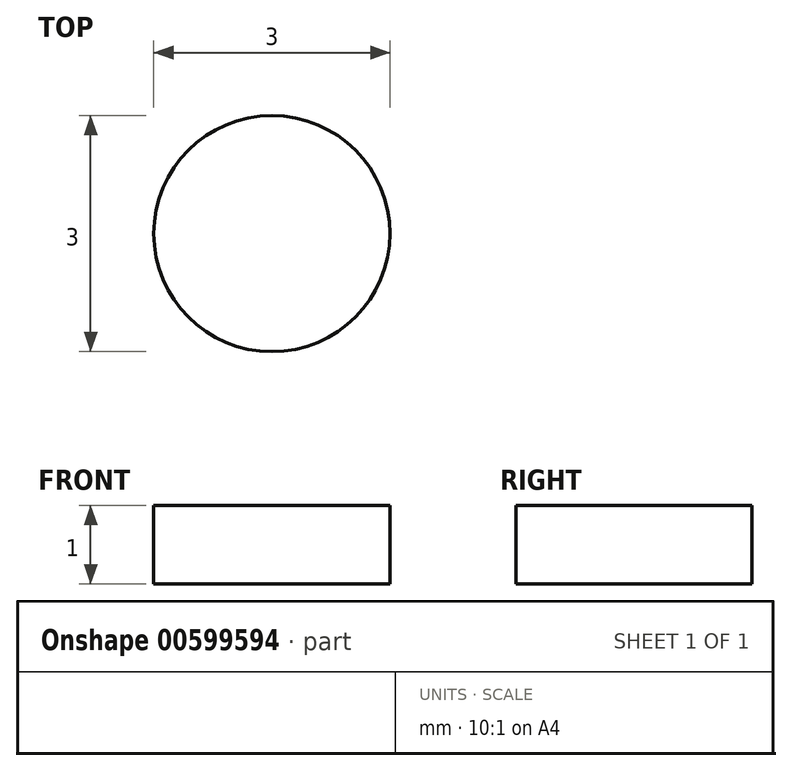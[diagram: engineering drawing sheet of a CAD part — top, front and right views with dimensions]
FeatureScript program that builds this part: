
annotation { "Feature Type Name" : "Feature", "Feature Type Description" : "" }
export const myFeature = defineFeature(function(context is Context, id is Id, definition is map)
    precondition{}
    {
        {
            var Q0;
            Q0=qCreatedBy(makeId("Top.planeOp"),FACE);
            var sketch = newSketch(context, id + "F0", { "sketchPlane" : qUnion([Q0])});
            skLineSegment(sketch, "E0.bottom", {"start": v(13.65, -7.45) * mm, "end": v(-13.65, -7.45) * mm});
            skLineSegment(sketch, "E0.top", {"start": v(13.65, 7.45) * mm, "end": v(-13.65, 7.45) * mm});
            skLineSegment(sketch, "E0.left", {"start": v(16.65, -4.45) * mm, "end": v(16.65, 4.45) * mm});
            skLineSegment(sketch, "E0.right", {"start": v(-16.65, -4.45) * mm, "end": v(-16.65, 4.45) * mm});
            skPoint(sketch, "E0.middle", {"position": v(0, 0) * mm});
            skPoint(sketch, "E1.visualSharp", {"position": v(16.65, 7.45) * mm});
            skArc(sketch, "E1.filletArc", {"start": v(16.65, 4.45) * mm, "mid": v(15.77, 6.57) * mm, "end": v(13.65, 7.45) * mm});
            skPoint(sketch, "E2.visualSharp", {"position": v(16.65, -7.45) * mm});
            skArc(sketch, "E2.filletArc", {"start": v(13.65, -7.45) * mm, "mid": v(15.77, -6.57) * mm, "end": v(16.65, -4.45) * mm});
            skPoint(sketch, "E3.visualSharp", {"position": v(-16.65, -7.45) * mm});
            skArc(sketch, "E3.filletArc", {"start": v(-16.65, -4.45) * mm, "mid": v(-15.77, -6.57) * mm, "end": v(-13.65, -7.45) * mm});
            skPoint(sketch, "E4.visualSharp", {"position": v(-16.65, 7.45) * mm});
            skArc(sketch, "E4.filletArc", {"start": v(-13.65, 7.45) * mm, "mid": v(-15.77, 6.57) * mm, "end": v(-16.65, 4.45) * mm});
            skSolve(sketch);
        }
        {
            var Q0;
            Q0=makeQuery(id+"F0.imprint","IMPRINT",FACE,{"disambiguationData":[TD([[makeQuery(id+"F0.imprint","IMPRINT",EDGE,{"derivedFrom":sQuery(id+"F0.wireOp",EDGE,"E0.bottom")}),-1.0]])]});
            extrude(context, id + "F1", {"entities" : qUnion([Q0]), "depth" : 8 * mm, "offsetDistance" : 25 * mm});
        }
        {
            var Q0;
            Q0=makeQuery(id+"F1.opExtrude","CAP_FACE",FACE,{"disambiguationData":[OSD([sQuery(id+"F0.wireOp",EDGE,"E0.bottom"),sQuery(id+"F0.wireOp",EDGE,"E0.top"),sQuery(id+"F0.wireOp",EDGE,"E0.left"),sQuery(id+"F0.wireOp",EDGE,"E0.right"),sQuery(id+"F0.wireOp",EDGE,"E1.filletArc"),sQuery(id+"F0.wireOp",EDGE,"E2.filletArc"),sQuery(id+"F0.wireOp",EDGE,"E3.filletArc"),sQuery(id+"F0.wireOp",EDGE,"E4.filletArc")])],"isStart":false});
            shell(context, id + "F2", {"entities" : qUnion([Q0]), "thickness" : 1 * mm});
        }
        {
            var Q0;
            Q0=makeQuery(id+"F1.opExtrude","CAP_FACE",FACE,{"disambiguationData":[OSD([sQuery(id+"F0.wireOp",EDGE,"E0.bottom"),sQuery(id+"F0.wireOp",EDGE,"E0.top"),sQuery(id+"F0.wireOp",EDGE,"E0.left"),sQuery(id+"F0.wireOp",EDGE,"E0.right"),sQuery(id+"F0.wireOp",EDGE,"E1.filletArc"),sQuery(id+"F0.wireOp",EDGE,"E2.filletArc"),sQuery(id+"F0.wireOp",EDGE,"E3.filletArc"),sQuery(id+"F0.wireOp",EDGE,"E4.filletArc")])],"isStart":true});
            var sketch = newSketch(context, id + "F3", { "sketchPlane" : qUnion([Q0])});
            skLineSegment(sketch, "E5.bottom", {"start": v(14.5, -8.25) * mm, "end": v(-14.5, -8.25) * mm});
            skLineSegment(sketch, "E5.top", {"start": v(14.5, 8.25) * mm, "end": v(-14.5, 8.25) * mm});
            skLineSegment(sketch, "E5.left", {"start": v(17.5, -5.25) * mm, "end": v(17.5, 5.25) * mm});
            skLineSegment(sketch, "E5.right", {"start": v(-17.5, -5.25) * mm, "end": v(-17.5, 5.25) * mm});
            skPoint(sketch, "E5.middle", {"position": v(0, 0) * mm});
            skPoint(sketch, "E6.visualSharp", {"position": v(17.5, 8.25) * mm});
            skArc(sketch, "E6.filletArc", {"start": v(17.5, 5.25) * mm, "mid": v(16.62, 7.37) * mm, "end": v(14.5, 8.25) * mm});
            skPoint(sketch, "E7.visualSharp", {"position": v(17.5, -8.25) * mm});
            skArc(sketch, "E7.filletArc", {"start": v(14.5, -8.25) * mm, "mid": v(16.62, -7.37) * mm, "end": v(17.5, -5.25) * mm});
            skPoint(sketch, "E8.visualSharp", {"position": v(-17.5, -8.25) * mm});
            skArc(sketch, "E8.filletArc", {"start": v(-17.5, -5.25) * mm, "mid": v(-16.62, -7.37) * mm, "end": v(-14.5, -8.25) * mm});
            skPoint(sketch, "E9.visualSharp", {"position": v(-17.5, 8.25) * mm});
            skArc(sketch, "E9.filletArc", {"start": v(-14.5, 8.25) * mm, "mid": v(-16.62, 7.37) * mm, "end": v(-17.5, 5.25) * mm});
            skSolve(sketch);
        }
        {
            var Q0;
            Q0=makeQuery(id+"F3.imprint","IMPRINT",FACE,{"disambiguationData":[TD([[makeQuery(id+"F3.imprint","IMPRINT",EDGE,{"derivedFrom":sQuery(id+"F3.wireOp",EDGE,"E5.bottom")}),-1.0]])]});
            extrude(context, id + "F4", {"entities" : qUnion([Q0]), "oppositeDirection" : true, "depth" : 1 * mm, "offsetDistance" : 25 * mm});
        }
        {
            var Q0;
            Q0=makeQuery(id+"F1.opExtrude","SWEPT_BODY",BODY,{"disambiguationData":[OSD([sQuery(id+"F0.wireOp",EDGE,"E0.bottom"),sQuery(id+"F0.wireOp",EDGE,"E0.top"),sQuery(id+"F0.wireOp",EDGE,"E0.left"),sQuery(id+"F0.wireOp",EDGE,"E0.right"),sQuery(id+"F0.wireOp",EDGE,"E1.filletArc"),sQuery(id+"F0.wireOp",EDGE,"E2.filletArc"),sQuery(id+"F0.wireOp",EDGE,"E3.filletArc"),sQuery(id+"F0.wireOp",EDGE,"E4.filletArc")])]});
            var Q1;
            Q1=makeQuery(id+"F4.opExtrude","SWEPT_BODY",BODY,{"disambiguationData":[OSD([sQuery(id+"F0.wireOp",EDGE,"E0.bottom"),sQuery(id+"F0.wireOp",EDGE,"E0.top"),sQuery(id+"F0.wireOp",EDGE,"E0.left"),sQuery(id+"F0.wireOp",EDGE,"E0.right"),sQuery(id+"F0.wireOp",EDGE,"E1.filletArc"),sQuery(id+"F0.wireOp",EDGE,"E2.filletArc"),sQuery(id+"F0.wireOp",EDGE,"E3.filletArc"),sQuery(id+"F0.wireOp",EDGE,"E4.filletArc"),sQuery(id+"F3.wireOp",EDGE,"E5.bottom"),sQuery(id+"F3.wireOp",EDGE,"E5.top"),sQuery(id+"F3.wireOp",EDGE,"E5.left"),sQuery(id+"F3.wireOp",EDGE,"E5.right"),sQuery(id+"F3.wireOp",EDGE,"E6.filletArc"),sQuery(id+"F3.wireOp",EDGE,"E7.filletArc"),sQuery(id+"F3.wireOp",EDGE,"E8.filletArc"),sQuery(id+"F3.wireOp",EDGE,"E9.filletArc")])]});
            booleanBodies(context, id + "F5", {"operationType" : BooleanOperationType.UNION, "tools" : qUnion([Q0, Q1])});
        }
        {
            var Q0;
            {var subQ0=sQuery(id+"F0.wireOp",EDGE,"E4.filletArc");var subQ1=sQuery(id+"F0.wireOp",EDGE,"E3.filletArc");var subQ2=sQuery(id+"F0.wireOp",EDGE,"E2.filletArc");var subQ3=sQuery(id+"F0.wireOp",EDGE,"E1.filletArc");var subQ4=sQuery(id+"F0.wireOp",EDGE,"E0.right");var subQ5=sQuery(id+"F0.wireOp",EDGE,"E0.left");var subQ6=sQuery(id+"F0.wireOp",EDGE,"E0.top");var subQ7=sQuery(id+"F0.wireOp",EDGE,"E0.bottom");Q0=makeQuery(id+"F5.opBoolean","MERGE",FACE,{"derivedFrom":[makeQuery(id+"F1.opExtrude","CAP_FACE",FACE,{"disambiguationData":[OSD([subQ7,subQ6,subQ5,subQ4,subQ3,subQ2,subQ1,subQ0])],"isStart":true}),makeQuery(id+"F4.opExtrude","CAP_FACE",FACE,{"disambiguationData":[OSD([subQ7,subQ6,subQ5,subQ4,subQ3,subQ2,subQ1,subQ0,sQuery(id+"F3.wireOp",EDGE,"E5.bottom"),sQuery(id+"F3.wireOp",EDGE,"E5.top"),sQuery(id+"F3.wireOp",EDGE,"E5.left"),sQuery(id+"F3.wireOp",EDGE,"E5.right"),sQuery(id+"F3.wireOp",EDGE,"E6.filletArc"),sQuery(id+"F3.wireOp",EDGE,"E7.filletArc"),sQuery(id+"F3.wireOp",EDGE,"E8.filletArc"),sQuery(id+"F3.wireOp",EDGE,"E9.filletArc")])],"isStart":true})]});}
            var sketch = newSketch(context, id + "F6", { "sketchPlane" : qUnion([Q0])});
            skCircle(sketch, "E10", {"center": v(2.5, 0.25) * mm, "radius": 1.5 * mm});
            skCircle(sketch, "E11.MirrorC", {"center": v(-2.5, 0.25) * mm, "radius": 1.5 * mm});
            skSolve(sketch);
        }
        {
            var Q0;
            Q0=makeQuery(id+"F6.imprint","IMPRINT",FACE,{"disambiguationData":[TD([[makeQuery(id+"F6.imprint","IMPRINT",EDGE,{"derivedFrom":sQuery(id+"F6.wireOp",EDGE,"E11.MirrorC")}),-1.0]])]});
            var Q1;
            Q1=makeQuery(id+"F6.imprint","IMPRINT",FACE,{"disambiguationData":[TD([[makeQuery(id+"F6.imprint","IMPRINT",EDGE,{"derivedFrom":sQuery(id+"F6.wireOp",EDGE,"E10")}),1.0]])]});
            extrude(context, id + "F7", {"entities" : qUnion([Q0, Q1]), "operationType" : NewBodyOperationType.REMOVE, "endBound" : BoundingType.THROUGH_ALL, "oppositeDirection" : true, "depth" : 25 * mm, "offsetDistance" : 25 * mm});
        }
    });
